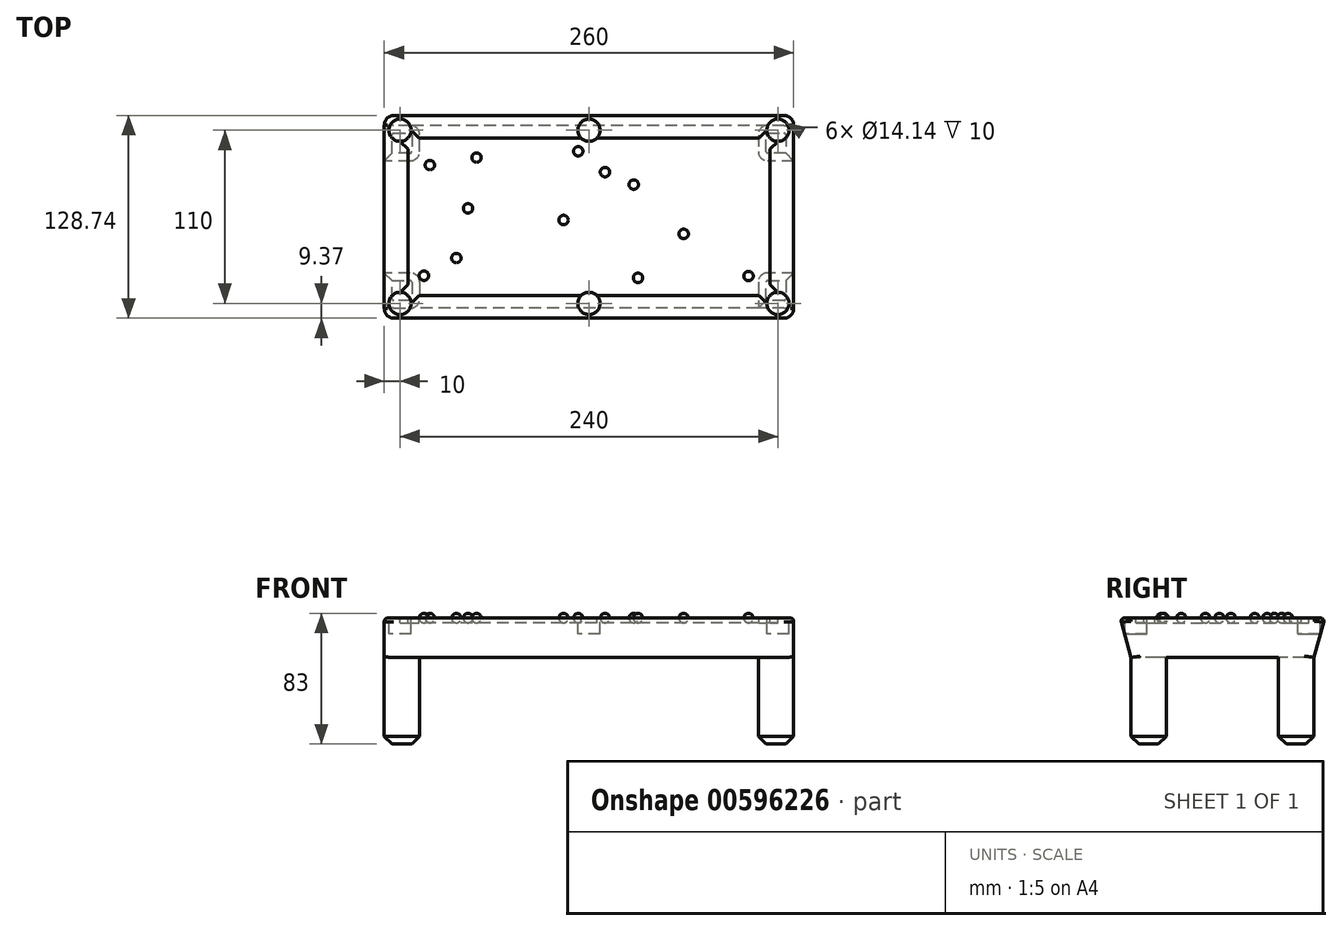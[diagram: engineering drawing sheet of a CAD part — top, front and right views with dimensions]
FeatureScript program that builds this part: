
annotation { "Feature Type Name" : "Feature", "Feature Type Description" : "" }
export const myFeature = defineFeature(function(context is Context, id is Id, definition is map)
    precondition{}
    {
        {
            var Q0;
            Q0=qCreatedBy(makeId("Top.planeOp"),FACE);
            var sketch = newSketch(context, id + "F0", { "sketchPlane" : qUnion([Q0])});
            skLineSegment(sketch, "E0.bottom", {"start": v(130, -65) * mm, "end": v(-130, -65) * mm});
            skLineSegment(sketch, "E0.top", {"start": v(130, 65) * mm, "end": v(-130, 65) * mm});
            skLineSegment(sketch, "E0.left", {"start": v(130, -65) * mm, "end": v(130, 65) * mm});
            skLineSegment(sketch, "E0.right", {"start": v(-130, -65) * mm, "end": v(-130, 65) * mm});
            skPoint(sketch, "E0.middle", {"position": v(0, 0) * mm});
            skLineSegment(sketch, "E1.bottom", {"start": v(112.93, -55) * mm, "end": v(7.07, -55) * mm});
            skLineSegment(sketch, "E1.top", {"start": v(112.93, 55) * mm, "end": v(7.07, 55) * mm});
            skLineSegment(sketch, "E1.left", {"start": v(120, -47.93) * mm, "end": v(120, 47.93) * mm});
            skLineSegment(sketch, "E1.right", {"start": v(-120, -47.93) * mm, "end": v(-120, 47.93) * mm});
            skLineSegment(sketch, "E2.bottom", {"start": v(107.93, -50) * mm, "end": v(5, -50) * mm});
            skLineSegment(sketch, "E2.top", {"start": v(107.93, 50) * mm, "end": v(5, 50) * mm});
            skLineSegment(sketch, "E2.left", {"start": v(115, -42.93) * mm, "end": v(115, 42.93) * mm});
            skLineSegment(sketch, "E2.right", {"start": v(-115, -42.93) * mm, "end": v(-115, 42.93) * mm});
            skCircle(sketch, "E3", {"center": v(120, 55) * mm, "radius": 7.07 * mm});
            skLineSegment(sketch, "E4", {"start": v(115, 42.93) * mm, "end": v(120, 47.93) * mm});
            skLineSegment(sketch, "E5", {"start": v(120, 47.93) * mm, "end": v(115, 42.93) * mm, "construction": true});
            skLineSegment(sketch, "E6", {"start": v(115, 42.93) * mm, "end": v(120, 42.93) * mm, "construction": true});
            skLineSegment(sketch, "E7", {"start": v(107.93, 50) * mm, "end": v(112.93, 55) * mm});
            skPoint(sketch, "E8.center.orphan", {"position": v(115, 50) * mm});
            skCircle(sketch, "E9", {"center": v(120, -55) * mm, "radius": 7.07 * mm});
            skCircle(sketch, "E10", {"center": v(-120, -55) * mm, "radius": 7.07 * mm});
            skCircle(sketch, "E11", {"center": v(-120, 55) * mm, "radius": 7.07 * mm});
            skCircle(sketch, "E12", {"center": v(0, -55) * mm, "radius": 7.07 * mm});
            skLineSegment(sketch, "E13", {"start": v(0, -47.93) * mm, "end": v(0, 47.93) * mm, "construction": true});
            skCircle(sketch, "E14", {"center": v(0, 55) * mm, "radius": 7.07 * mm});
            skLineSegment(sketch, "E15.trimOffspring", {"start": v(-7.07, 55) * mm, "end": v(-112.93, 55) * mm});
            skLineSegment(sketch, "E16.trimOffspring", {"start": v(-5, 50) * mm, "end": v(-107.93, 50) * mm});
            skLineSegment(sketch, "E17.trimOffspring", {"start": v(-7.07, -55) * mm, "end": v(-112.93, -55) * mm});
            skLineSegment(sketch, "E18.trimOffspring", {"start": v(-5, -50) * mm, "end": v(-107.93, -50) * mm});
            skLineSegment(sketch, "E19", {"start": v(107.93, -50) * mm, "end": v(112.93, -55) * mm});
            skLineSegment(sketch, "E20", {"start": v(115, -42.93) * mm, "end": v(120, -47.93) * mm});
            skLineSegment(sketch, "E21", {"start": v(-120, -47.93) * mm, "end": v(-115, -42.93) * mm});
            skLineSegment(sketch, "E22", {"start": v(-112.93, -55) * mm, "end": v(-107.93, -50) * mm});
            skPoint(sketch, "E23.orphan", {"position": v(-115, -50) * mm});
            skLineSegment(sketch, "E24", {"start": v(-120, 47.93) * mm, "end": v(-115, 42.93) * mm});
            skLineSegment(sketch, "E25", {"start": v(-112.93, 55) * mm, "end": v(-107.93, 50) * mm});
            skSolve(sketch);
        }
        {
            var Q0;
            Q0=qCreatedBy(makeId("Right.planeOp"),FACE);
            var sketch = newSketch(context, id + "F1", { "sketchPlane" : qUnion([Q0])});
            skLineSegment(sketch, "E26", {"start": v(58.07, -25) * mm, "end": v(-58.07, -25) * mm});
            skLineSegment(sketch, "E27.0", {"start": v(-65, 0) * mm, "end": v(65, 0) * mm});
            skLineSegment(sketch, "E28", {"start": v(58.07, -25) * mm, "end": v(65, 0) * mm});
            skLineSegment(sketch, "E29", {"start": v(-58.07, -25) * mm, "end": v(-65, 0) * mm});
            skLineSegment(sketch, "E30", {"start": v(58.07, -25) * mm, "end": v(58.07, -80) * mm});
            skLineSegment(sketch, "E31", {"start": v(58.07, -80) * mm, "end": v(-58.07, -80) * mm});
            skLineSegment(sketch, "E32", {"start": v(-58.07, -80) * mm, "end": v(-58.07, -25) * mm});
            skSolve(sketch);
        }
        {
            var Q0;
            Q0=makeQuery(id+"F1.imprint","IMPRINT",FACE,{"disambiguationData":[TD([[makeQuery(id+"F1.imprint","IMPRINT",EDGE,{"derivedFrom":sQuery(id+"F1.wireOp",EDGE,"E26")}),1.0]])]});
            var Q1;
            Q1=makeQuery(id+"F1.imprint","IMPRINT",FACE,{"disambiguationData":[TD([[makeQuery(id+"F1.imprint","IMPRINT",EDGE,{"derivedFrom":sQuery(id+"F1.wireOp",EDGE,"E26")}),-1.0]])]});
            extrude(context, id + "F2", {"entities" : qUnion([Q0, Q1]), "endBound" : BoundingType.SYMMETRIC, "depth" : 260 * mm, "offsetDistance" : 25 * mm});
        }
        {
            var Q0;
            Q0=makeQuery(id+"F2.opExtrude","SWEPT_FACE",FACE,{"disambiguationData":[OSD([sQuery(id+"F1.wireOp",EDGE,"E32")])]});
            var sketch = newSketch(context, id + "F3", { "sketchPlane" : qUnion([Q0])});
            skLineSegment(sketch, "E33.0", {"start": v(130, -80) * mm, "end": v(-130, -80) * mm});
            skLineSegment(sketch, "E34.0", {"start": v(130, -25) * mm, "end": v(-130, -25) * mm});
            skLineSegment(sketch, "E35", {"start": v(-107.5, -80) * mm, "end": v(-107.5, -25) * mm});
            skLineSegment(sketch, "E36", {"start": v(107.5, -80) * mm, "end": v(107.5, -25) * mm});
            skSolve(sketch);
        }
        {
            var Q0;
            {var subQ0=sQuery(id+"F3.wireOp",EDGE,"E35");Q0=makeQuery(id+"F3.imprint","IMPRINT",FACE,{"disambiguationData":[TD([[makeQuery(id+"F3.imprint","IMPRINT",EDGE,{"derivedFrom":subQ0}),-1.0]])]});}
            extrude(context, id + "F4", {"entities" : qUnion([Q0]), "operationType" : NewBodyOperationType.REMOVE, "oppositeDirection" : true, "depth" : 130 * mm, "offsetDistance" : 25 * mm});
        }
        {
            var Q0;
            Q0=makeQuery(id+"F2.opExtrude","CAP_FACE",FACE,{"disambiguationData":[OSD([sQuery(id+"F1.wireOp",EDGE,"E27.0"),sQuery(id+"F1.wireOp",EDGE,"E28"),sQuery(id+"F1.wireOp",EDGE,"E29"),sQuery(id+"F1.wireOp",EDGE,"E30"),sQuery(id+"F1.wireOp",EDGE,"E31"),sQuery(id+"F1.wireOp",EDGE,"E32")])],"isStart":true});
            var sketch = newSketch(context, id + "F5", { "sketchPlane" : qUnion([Q0])});
            skLineSegment(sketch, "E37.0", {"start": v(-58.07, -80) * mm, "end": v(58.07, -80) * mm});
            skLineSegment(sketch, "E38.0.0", {"start": v(58.07, -80) * mm, "end": v(58.07, -25) * mm});
            skLineSegment(sketch, "E38.0.1", {"start": v(58.07, -25) * mm, "end": v(65, 0) * mm});
            skLineSegment(sketch, "E38.0.2", {"start": v(65, 0) * mm, "end": v(-65, 0) * mm});
            skLineSegment(sketch, "E38.0.3", {"start": v(-65, 0) * mm, "end": v(-58.07, -25) * mm});
            skLineSegment(sketch, "E38.0.4", {"start": v(-58.07, -25) * mm, "end": v(-58.07, -80) * mm});
            skLineSegment(sketch, "E39", {"start": v(-58.07, -25) * mm, "end": v(58.07, -25) * mm});
            skLineSegment(sketch, "E40", {"start": v(-35.57, -80) * mm, "end": v(-35.57, -25) * mm});
            skLineSegment(sketch, "E41", {"start": v(35.57, -80) * mm, "end": v(35.57, -25) * mm});
            skSolve(sketch);
        }
        {
            var Q0;
            {var subQ0=sQuery(id+"F5.wireOp",EDGE,"E40");Q0=makeQuery(id+"F5.imprint","IMPRINT",FACE,{"disambiguationData":[TD([[makeQuery(id+"F5.imprint","IMPRINT",EDGE,{"derivedFrom":subQ0}),-1.0]])]});}
            extrude(context, id + "F6", {"entities" : qUnion([Q0]), "operationType" : NewBodyOperationType.REMOVE, "oppositeDirection" : true, "depth" : 260 * mm, "offsetDistance" : 25 * mm});
        }
        {
            var Q0;
            {var subQ0=sQuery(id+"F0.wireOp",EDGE,"E9");var subQ1=makeQuery(id+"F0.imprint","INTERSECT",VERTEX,{"derivedFrom":[sQuery(id+"F0.wireOp",EDGE,"E1.bottom"),subQ0,sQuery(id+"F0.wireOp",EDGE,"E19")]});Q0=makeQuery(id+"F0.imprint","IMPRINT",FACE,{"disambiguationData":[TD([[makeQuery(id+"F0.imprint","IMPRINT",EDGE,{"disambiguationData":[TD([[subQ1,1.0]])],"derivedFrom":subQ0}),1.0]])]});}
            var Q1;
            {var subQ0=sQuery(id+"F0.wireOp",EDGE,"E3");var subQ1=makeQuery(id+"F0.imprint","INTERSECT",VERTEX,{"derivedFrom":[sQuery(id+"F0.wireOp",EDGE,"E1.top"),subQ0,sQuery(id+"F0.wireOp",EDGE,"E7")]});Q1=makeQuery(id+"F0.imprint","IMPRINT",FACE,{"disambiguationData":[TD([[makeQuery(id+"F0.imprint","IMPRINT",EDGE,{"disambiguationData":[TD([[subQ1,-1.0]])],"derivedFrom":subQ0}),1.0]])]});}
            var Q2;
            {var subQ0=sQuery(id+"F0.wireOp",EDGE,"E14");var subQ1=makeQuery(id+"F0.imprint","INTERSECT",VERTEX,{"derivedFrom":[sQuery(id+"F0.wireOp",EDGE,"E1.top"),subQ0]});Q2=makeQuery(id+"F0.imprint","IMPRINT",FACE,{"disambiguationData":[TD([[makeQuery(id+"F0.imprint","IMPRINT",EDGE,{"disambiguationData":[TD([[subQ1,-1.0]])],"derivedFrom":subQ0}),1.0]])]});}
            var Q3;
            {var subQ0=sQuery(id+"F0.wireOp",EDGE,"E12");var subQ1=makeQuery(id+"F0.imprint","INTERSECT",VERTEX,{"derivedFrom":[sQuery(id+"F0.wireOp",EDGE,"E1.bottom"),subQ0]});Q3=makeQuery(id+"F0.imprint","IMPRINT",FACE,{"disambiguationData":[TD([[makeQuery(id+"F0.imprint","IMPRINT",EDGE,{"disambiguationData":[TD([[subQ1,-1.0]])],"derivedFrom":subQ0}),1.0]])]});}
            var Q4;
            {var subQ0=sQuery(id+"F0.wireOp",EDGE,"E10");var subQ1=makeQuery(id+"F0.imprint","INTERSECT",VERTEX,{"derivedFrom":[sQuery(id+"F0.wireOp",EDGE,"E1.right"),subQ0,sQuery(id+"F0.wireOp",EDGE,"E21")]});Q4=makeQuery(id+"F0.imprint","IMPRINT",FACE,{"disambiguationData":[TD([[makeQuery(id+"F0.imprint","IMPRINT",EDGE,{"disambiguationData":[TD([[subQ1,1.0]])],"derivedFrom":subQ0}),1.0]])]});}
            var Q5;
            {var subQ0=sQuery(id+"F0.wireOp",EDGE,"E11");var subQ1=makeQuery(id+"F0.imprint","INTERSECT",VERTEX,{"derivedFrom":[sQuery(id+"F0.wireOp",EDGE,"E1.right"),subQ0,sQuery(id+"F0.wireOp",EDGE,"E24")]});Q5=makeQuery(id+"F0.imprint","IMPRINT",FACE,{"disambiguationData":[TD([[makeQuery(id+"F0.imprint","IMPRINT",EDGE,{"disambiguationData":[TD([[subQ1,1.0]])],"derivedFrom":subQ0}),1.0]])]});}
            extrude(context, id + "F7", {"entities" : qUnion([Q0, Q1, Q2, Q3, Q4, Q5]), "operationType" : NewBodyOperationType.REMOVE, "oppositeDirection" : true, "depth" : 10 * mm, "offsetDistance" : 25 * mm});
        }
        {
            var Q0;
            {var subQ13=sQuery(id+"F0.wireOp",EDGE,"E2.bottom");Q0=makeQuery(id+"F0.imprint","IMPRINT",FACE,{"disambiguationData":[TD([[makeQuery(id+"F0.imprint","IMPRINT",EDGE,{"derivedFrom":subQ13}),-1.0]])]});}
            extrude(context, id + "F8", {"entities" : qUnion([Q0]), "operationType" : NewBodyOperationType.REMOVE, "oppositeDirection" : true, "depth" : 3 * mm, "offsetDistance" : 25 * mm});
        }
        {
            var Q0;
            Q0=makeQuery(id+"F2.opExtrude","CAP_EDGE",EDGE,{"disambiguationData":[OSD([sQuery(id+"F1.wireOp",EDGE,"E28")])],"isStart":false});
            fillet(context, id + "F9", {"entities" : qUnion([Q0]), "radius" : 6 * mm, "tangentPropagation" : true, "allowEdgeOverflow" : false});
        }
        {
            var Q0;
            Q0=makeQuery(id+"F2.opExtrude","CAP_EDGE",EDGE,{"disambiguationData":[OSD([sQuery(id+"F1.wireOp",EDGE,"E29")])],"isStart":false});
            var Q1;
            Q1=makeQuery(id+"F2.opExtrude","CAP_EDGE",EDGE,{"disambiguationData":[OSD([sQuery(id+"F1.wireOp",EDGE,"E29")])],"isStart":true});
            var Q2;
            Q2=makeQuery(id+"F2.opExtrude","CAP_EDGE",EDGE,{"disambiguationData":[OSD([sQuery(id+"F1.wireOp",EDGE,"E28")])],"isStart":true});
            fillet(context, id + "F10", {"entities" : qUnion([Q0, Q1, Q2]), "radius" : 6 * mm, "tangentPropagation" : true, "allowEdgeOverflow" : false});
        }
        {
            var Q0;
            Q0=makeQuery(id+"F2.opExtrude","CAP_EDGE",EDGE,{"disambiguationData":[OSD([sQuery(id+"F1.wireOp",EDGE,"E32")])],"isStart":false});
            var Q1;
            Q1=makeQuery(id+"F2.opExtrude","CAP_EDGE",EDGE,{"disambiguationData":[OSD([sQuery(id+"F1.wireOp",EDGE,"E30")])],"isStart":false});
            var Q2;
            Q2=makeQuery(id+"F2.opExtrude","CAP_EDGE",EDGE,{"disambiguationData":[OSD([sQuery(id+"F1.wireOp",EDGE,"E32")])],"isStart":true});
            var Q3;
            Q3=makeQuery(id+"F2.opExtrude","CAP_EDGE",EDGE,{"disambiguationData":[OSD([sQuery(id+"F1.wireOp",EDGE,"E30")])],"isStart":true});
            fillet(context, id + "F11", {"entities" : qUnion([Q0, Q1, Q2, Q3]), "radius" : 6 * mm, "tangentPropagation" : true, "allowEdgeOverflow" : false});
        }
        {
            var Q0;
            Q0=makeQuery(id+"F2.opExtrude","SWEPT_EDGE",EDGE,{"disambiguationData":[OSD([sQuery(id+"F1.wireOp",EDGE,"E27.0"),sQuery(id+"F1.wireOp",EDGE,"E29")])]});
            var Q1;
            Q1=makeQuery(id+"F2.opExtrude","CAP_EDGE",EDGE,{"disambiguationData":[OSD([sQuery(id+"F1.wireOp",EDGE,"E27.0")])],"isStart":true});
            fillet(context, id + "F12", {"entities" : qUnion([Q0, Q1]), "radius" : 2 * mm, "tangentPropagation" : true, "allowEdgeOverflow" : false});
        }
        {
            var Q0;
            Q0=qCreatedBy(makeId("Top.planeOp"),FACE);
            var sketch = newSketch(context, id + "F13", { "sketchPlane" : qUnion([Q0])});
            skCircle(sketch, "E42", {"center": v(-71.42, 37.6) * mm, "radius": 3 * mm});
            skLineSegment(sketch, "E43", {"start": v(-71.42, 34.6) * mm, "end": v(-71.42, 40.6) * mm});
            skCircle(sketch, "E44", {"center": v(-84.23, -26.2) * mm, "radius": 3 * mm});
            skLineSegment(sketch, "E45", {"start": v(-84.23, -29.2) * mm, "end": v(-84.23, -23.2) * mm});
            skCircle(sketch, "E46", {"center": v(31.13, -38.8) * mm, "radius": 3 * mm});
            skLineSegment(sketch, "E47", {"start": v(31.13, -41.8) * mm, "end": v(31.13, -35.8) * mm});
            skCircle(sketch, "E48", {"center": v(-16.15, -2.03) * mm, "radius": 3 * mm});
            skLineSegment(sketch, "E49", {"start": v(-16.15, -5.03) * mm, "end": v(-16.15, 0.97) * mm});
            skCircle(sketch, "E50", {"center": v(28.4, 20.46) * mm, "radius": 3 * mm});
            skLineSegment(sketch, "E51", {"start": v(28.4, 17.46) * mm, "end": v(28.4, 23.46) * mm});
            skCircle(sketch, "E52", {"center": v(-6.85, 41.64) * mm, "radius": 3 * mm});
            skLineSegment(sketch, "E53", {"start": v(-6.85, 38.64) * mm, "end": v(-6.85, 44.64) * mm});
            skCircle(sketch, "E54", {"center": v(101.35, -37.6) * mm, "radius": 3 * mm});
            skLineSegment(sketch, "E55", {"start": v(101.35, -40.6) * mm, "end": v(101.35, -34.6) * mm});
            skCircle(sketch, "E56", {"center": v(-101.07, 32.85) * mm, "radius": 3 * mm});
            skLineSegment(sketch, "E57", {"start": v(-101.07, 29.85) * mm, "end": v(-101.07, 35.85) * mm});
            skCircle(sketch, "E58", {"center": v(-104.83, -37.39) * mm, "radius": 3 * mm});
            skLineSegment(sketch, "E59", {"start": v(-104.83, -40.39) * mm, "end": v(-104.83, -34.39) * mm});
            skCircle(sketch, "E60", {"center": v(10.14, 28.37) * mm, "radius": 3 * mm});
            skLineSegment(sketch, "E61", {"start": v(10.14, 25.37) * mm, "end": v(10.14, 31.37) * mm});
            skCircle(sketch, "E62", {"center": v(-76.83, 5.36) * mm, "radius": 3 * mm});
            skLineSegment(sketch, "E63", {"start": v(-76.83, 2.36) * mm, "end": v(-76.83, 8.36) * mm});
            skCircle(sketch, "E64", {"center": v(60.12, -10.86) * mm, "radius": 3 * mm});
            skLineSegment(sketch, "E65", {"start": v(60.12, -13.86) * mm, "end": v(60.12, -7.86) * mm});
            skSolve(sketch);
        }
        {
            var Q0;
            {var subQ0=sQuery(id+"F13.wireOp",EDGE,"E43");Q0=makeQuery(id+"F13.imprint","IMPRINT",FACE,{"disambiguationData":[TD([[makeQuery(id+"F13.imprint","IMPRINT",EDGE,{"derivedFrom":subQ0}),-1.0]])]});}
            var Q1;
            Q1=sQuery(id+"F13.wireOp",EDGE,"E43");
            revolve(context, id + "F14", {"entities" : qUnion([Q0]), "axis" : qUnion([Q1]), "revolveType" : RevolveType.FULL});
        }
        {
            var Q0;
            {var subQ0=sQuery(id+"F13.wireOp",EDGE,"E49");Q0=makeQuery(id+"F13.imprint","IMPRINT",FACE,{"disambiguationData":[TD([[makeQuery(id+"F13.imprint","IMPRINT",EDGE,{"derivedFrom":subQ0}),-1.0]])]});}
            var Q1;
            Q1=sQuery(id+"F13.wireOp",EDGE,"E49");
            revolve(context, id + "F15", {"entities" : qUnion([Q0]), "axis" : qUnion([Q1]), "revolveType" : RevolveType.FULL});
        }
        {
            var Q0;
            {var subQ0=sQuery(id+"F13.wireOp",EDGE,"E63");Q0=makeQuery(id+"F13.imprint","IMPRINT",FACE,{"disambiguationData":[TD([[makeQuery(id+"F13.imprint","IMPRINT",EDGE,{"derivedFrom":subQ0}),-1.0]])]});}
            var Q1;
            Q1=sQuery(id+"F13.wireOp",EDGE,"E56");
            var Q2;
            Q2=sQuery(id+"F13.wireOp",EDGE,"E63");
            revolve(context, id + "F16", {"entities" : qUnion([Q0]), "surfaceEntities" : qUnion([Q1]), "axis" : qUnion([Q2]), "revolveType" : RevolveType.FULL});
        }
        {
            var Q0;
            {var subQ0=sQuery(id+"F13.wireOp",EDGE,"E53");Q0=makeQuery(id+"F13.imprint","IMPRINT",FACE,{"disambiguationData":[TD([[makeQuery(id+"F13.imprint","IMPRINT",EDGE,{"derivedFrom":subQ0}),-1.0]])]});}
            var Q1;
            Q1=sQuery(id+"F13.wireOp",EDGE,"E53");
            revolve(context, id + "F17", {"entities" : qUnion([Q0]), "axis" : qUnion([Q1]), "revolveType" : RevolveType.FULL});
        }
        {
            var Q0;
            {var subQ0=sQuery(id+"F13.wireOp",EDGE,"E51");Q0=makeQuery(id+"F13.imprint","IMPRINT",FACE,{"disambiguationData":[TD([[makeQuery(id+"F13.imprint","IMPRINT",EDGE,{"derivedFrom":subQ0}),-1.0]])]});}
            var Q1;
            Q1=sQuery(id+"F13.wireOp",EDGE,"E51");
            revolve(context, id + "F18", {"entities" : qUnion([Q0]), "axis" : qUnion([Q1]), "revolveType" : RevolveType.FULL});
        }
        {
            var Q0;
            {var subQ0=sQuery(id+"F13.wireOp",EDGE,"E47");Q0=makeQuery(id+"F13.imprint","IMPRINT",FACE,{"disambiguationData":[TD([[makeQuery(id+"F13.imprint","IMPRINT",EDGE,{"derivedFrom":subQ0}),-1.0]])]});}
            var Q1;
            Q1=sQuery(id+"F13.wireOp",EDGE,"E47");
            revolve(context, id + "F19", {"entities" : qUnion([Q0]), "axis" : qUnion([Q1]), "revolveType" : RevolveType.FULL});
        }
        {
            var Q0;
            {var subQ0=sQuery(id+"F13.wireOp",EDGE,"E55");Q0=makeQuery(id+"F13.imprint","IMPRINT",FACE,{"disambiguationData":[TD([[makeQuery(id+"F13.imprint","IMPRINT",EDGE,{"derivedFrom":subQ0}),1.0]])]});}
            var Q1;
            Q1=sQuery(id+"F13.wireOp",EDGE,"E55");
            revolve(context, id + "F20", {"entities" : qUnion([Q0]), "axis" : qUnion([Q1]), "revolveType" : RevolveType.FULL});
        }
        {
            var Q0;
            {var subQ0=sQuery(id+"F13.wireOp",EDGE,"E45");Q0=makeQuery(id+"F13.imprint","IMPRINT",FACE,{"disambiguationData":[TD([[makeQuery(id+"F13.imprint","IMPRINT",EDGE,{"derivedFrom":subQ0}),1.0]])]});}
            var Q1;
            Q1=sQuery(id+"F13.wireOp",EDGE,"E45");
            revolve(context, id + "F21", {"entities" : qUnion([Q0]), "axis" : qUnion([Q1]), "revolveType" : RevolveType.FULL});
        }
        {
            var Q0;
            {var subQ0=sQuery(id+"F13.wireOp",EDGE,"E61");Q0=makeQuery(id+"F13.imprint","IMPRINT",FACE,{"disambiguationData":[TD([[makeQuery(id+"F13.imprint","IMPRINT",EDGE,{"derivedFrom":subQ0}),-1.0]])]});}
            var Q1;
            Q1=sQuery(id+"F13.wireOp",EDGE,"E61");
            revolve(context, id + "F22", {"entities" : qUnion([Q0]), "axis" : qUnion([Q1]), "revolveType" : RevolveType.FULL});
        }
        {
            var Q0;
            {var subQ0=sQuery(id+"F13.wireOp",EDGE,"E57");Q0=makeQuery(id+"F13.imprint","IMPRINT",FACE,{"disambiguationData":[TD([[makeQuery(id+"F13.imprint","IMPRINT",EDGE,{"derivedFrom":subQ0}),1.0]])]});}
            var Q1;
            Q1=sQuery(id+"F13.wireOp",EDGE,"E57");
            revolve(context, id + "F23", {"entities" : qUnion([Q0]), "axis" : qUnion([Q1]), "revolveType" : RevolveType.FULL});
        }
        {
            var Q0;
            {var subQ0=sQuery(id+"F13.wireOp",EDGE,"E65");Q0=makeQuery(id+"F13.imprint","IMPRINT",FACE,{"disambiguationData":[TD([[makeQuery(id+"F13.imprint","IMPRINT",EDGE,{"derivedFrom":subQ0}),1.0]])]});}
            var Q1;
            Q1=sQuery(id+"F13.wireOp",EDGE,"E65");
            revolve(context, id + "F24", {"entities" : qUnion([Q0]), "axis" : qUnion([Q1]), "revolveType" : RevolveType.FULL});
        }
        {
            var Q0;
            {var subQ0=sQuery(id+"F13.wireOp",EDGE,"E59");Q0=makeQuery(id+"F13.imprint","IMPRINT",FACE,{"disambiguationData":[TD([[makeQuery(id+"F13.imprint","IMPRINT",EDGE,{"derivedFrom":subQ0}),-1.0]])]});}
            var Q1;
            Q1=sQuery(id+"F13.wireOp",EDGE,"E59");
            revolve(context, id + "F25", {"entities" : qUnion([Q0]), "axis" : qUnion([Q1]), "revolveType" : RevolveType.FULL});
        }
        {
            var Q0;
            Q0=makeQuery(id+"F4.boolean.opBoolean","COPY",EDGE,{"derivedFrom":makeQuery(id+"F4.opExtrude","CAP_EDGE",EDGE,{"disambiguationData":[OSD([sQuery(id+"F3.wireOp",EDGE,"E35")])],"isStart":true})});
            var Q1;
            Q1=makeQuery(id+"F6.boolean.opBoolean","INTERSECT",EDGE,{"derivedFrom":[makeQuery(id+"F4.boolean.opBoolean","COPY",FACE,{"derivedFrom":makeQuery(id+"F4.opExtrude","SWEPT_FACE",FACE,{"disambiguationData":[OSD([sQuery(id+"F3.wireOp",EDGE,"E35")])]})}),makeQuery(id+"F6.opExtrude","SWEPT_FACE",FACE,{"disambiguationData":[OSD([sQuery(id+"F5.wireOp",EDGE,"E41")])]})]});
            var Q2;
            Q2=makeQuery(id+"F6.boolean.opBoolean","INTERSECT",EDGE,{"derivedFrom":[makeQuery(id+"F4.boolean.opBoolean","COPY",FACE,{"derivedFrom":makeQuery(id+"F4.opExtrude","SWEPT_FACE",FACE,{"disambiguationData":[OSD([sQuery(id+"F3.wireOp",EDGE,"E35")])]})}),makeQuery(id+"F6.opExtrude","SWEPT_FACE",FACE,{"disambiguationData":[OSD([sQuery(id+"F5.wireOp",EDGE,"E40")])]})]});
            var Q3;
            Q3=makeQuery(id+"F6.boolean.opBoolean","COPY",EDGE,{"derivedFrom":makeQuery(id+"F6.opExtrude","CAP_EDGE",EDGE,{"disambiguationData":[OSD([sQuery(id+"F5.wireOp",EDGE,"E40")])],"isStart":true})});
            var Q4;
            Q4=makeQuery(id+"F4.boolean.opBoolean","INTERSECT",EDGE,{"derivedFrom":[makeQuery(id+"F2.opExtrude","SWEPT_FACE",FACE,{"disambiguationData":[OSD([sQuery(id+"F1.wireOp",EDGE,"E30")])]}),makeQuery(id+"F4.opExtrude","SWEPT_FACE",FACE,{"disambiguationData":[OSD([sQuery(id+"F3.wireOp",EDGE,"E35")])]})]});
            var Q5;
            Q5=makeQuery(id+"F4.boolean.opBoolean","COPY",EDGE,{"derivedFrom":makeQuery(id+"F4.opExtrude","CAP_EDGE",EDGE,{"disambiguationData":[OSD([sQuery(id+"F3.wireOp",EDGE,"E36")])],"isStart":true})});
            var Q6;
            Q6=makeQuery(id+"F6.boolean.opBoolean","COPY",EDGE,{"derivedFrom":makeQuery(id+"F6.opExtrude","CAP_EDGE",EDGE,{"disambiguationData":[OSD([sQuery(id+"F5.wireOp",EDGE,"E41")])],"isStart":false})});
            var Q7;
            Q7=makeQuery(id+"F6.boolean.opBoolean","INTERSECT",EDGE,{"derivedFrom":[makeQuery(id+"F4.boolean.opBoolean","COPY",FACE,{"derivedFrom":makeQuery(id+"F4.opExtrude","SWEPT_FACE",FACE,{"disambiguationData":[OSD([sQuery(id+"F3.wireOp",EDGE,"E36")])]})}),makeQuery(id+"F6.opExtrude","SWEPT_FACE",FACE,{"disambiguationData":[OSD([sQuery(id+"F5.wireOp",EDGE,"E40")])]})]});
            var Q8;
            Q8=makeQuery(id+"F6.boolean.opBoolean","COPY",EDGE,{"derivedFrom":makeQuery(id+"F6.opExtrude","CAP_EDGE",EDGE,{"disambiguationData":[OSD([sQuery(id+"F5.wireOp",EDGE,"E40")])],"isStart":false})});
            var Q9;
            Q9=makeQuery(id+"F6.boolean.opBoolean","INTERSECT",EDGE,{"derivedFrom":[makeQuery(id+"F4.boolean.opBoolean","COPY",FACE,{"derivedFrom":makeQuery(id+"F4.opExtrude","SWEPT_FACE",FACE,{"disambiguationData":[OSD([sQuery(id+"F3.wireOp",EDGE,"E36")])]})}),makeQuery(id+"F6.opExtrude","SWEPT_FACE",FACE,{"disambiguationData":[OSD([sQuery(id+"F5.wireOp",EDGE,"E41")])]})]});
            var Q10;
            Q10=makeQuery(id+"F4.boolean.opBoolean","INTERSECT",EDGE,{"derivedFrom":[makeQuery(id+"F2.opExtrude","SWEPT_FACE",FACE,{"disambiguationData":[OSD([sQuery(id+"F1.wireOp",EDGE,"E30")])]}),makeQuery(id+"F4.opExtrude","SWEPT_FACE",FACE,{"disambiguationData":[OSD([sQuery(id+"F3.wireOp",EDGE,"E36")])]})]});
            var Q11;
            Q11=makeQuery(id+"F6.boolean.opBoolean","COPY",EDGE,{"derivedFrom":makeQuery(id+"F6.opExtrude","CAP_EDGE",EDGE,{"disambiguationData":[OSD([sQuery(id+"F5.wireOp",EDGE,"E41")])],"isStart":true})});
            fillet(context, id + "F26", {"entities" : qUnion([Q0, Q1, Q2, Q3, Q4, Q5, Q6, Q7, Q8, Q9, Q10, Q11]), "radius" : 6 * mm, "tangentPropagation" : true, "allowEdgeOverflow" : false});
        }
        {
            var Q0;
            {var subQ0=sQuery(id+"F1.wireOp",EDGE,"E32");var subQ1=sQuery(id+"F1.wireOp",EDGE,"E31");var subQ4=makeQuery(id+"F2.opExtrude","SWEPT_FACE",FACE,{"disambiguationData":[OSD([subQ0])]});var subQ5=makeQuery(id+"F4.opExtrude","SWEPT_FACE",FACE,{"disambiguationData":[OSD([sQuery(id+"F3.wireOp",EDGE,"E36")])]});Q0=makeQuery(id+"F6.boolean.opBoolean","SPLIT",FACE,{"disambiguationData":[TD([subQ4])],"derivedFrom":makeQuery(id+"F4.boolean.opBoolean","SPLIT",FACE,{"disambiguationData":[TD([subQ5])],"derivedFrom":makeQuery(id+"F2.opExtrude","SWEPT_FACE",FACE,{"disambiguationData":[OSD([subQ1])]})})});}
            var Q1;
            {var subQ0=sQuery(id+"F1.wireOp",EDGE,"E32");var subQ1=sQuery(id+"F1.wireOp",EDGE,"E31");var subQ4=makeQuery(id+"F2.opExtrude","SWEPT_FACE",FACE,{"disambiguationData":[OSD([subQ0])]});var subQ5=makeQuery(id+"F4.opExtrude","SWEPT_FACE",FACE,{"disambiguationData":[OSD([sQuery(id+"F3.wireOp",EDGE,"E35")])]});Q1=makeQuery(id+"F6.boolean.opBoolean","SPLIT",FACE,{"disambiguationData":[TD([subQ4])],"derivedFrom":makeQuery(id+"F4.boolean.opBoolean","SPLIT",FACE,{"disambiguationData":[TD([subQ5])],"derivedFrom":makeQuery(id+"F2.opExtrude","SWEPT_FACE",FACE,{"disambiguationData":[OSD([subQ1])]})})});}
            var Q2;
            {var subQ1=sQuery(id+"F5.wireOp",EDGE,"E40");Q2=makeQuery(id+"F6.boolean.opBoolean","COPY",EDGE,{"disambiguationData":[TD([makeQuery(id+"F4.boolean.opBoolean","COPY",FACE,{"derivedFrom":makeQuery(id+"F4.opExtrude","SWEPT_FACE",FACE,{"disambiguationData":[OSD([sQuery(id+"F3.wireOp",EDGE,"E35")])]})})])],"derivedFrom":makeQuery(id+"F6.opExtrude","SWEPT_EDGE",EDGE,{"disambiguationData":[OSD([sQuery(id+"F5.wireOp",EDGE,"E37.0"),subQ1])]})});}
            var Q3;
            {var subQ1=sQuery(id+"F1.wireOp",EDGE,"E31");var subQ2=sQuery(id+"F1.wireOp",EDGE,"E30");var subQ4=makeQuery(id+"F2.opExtrude","SWEPT_FACE",FACE,{"disambiguationData":[OSD([subQ2])]});var subQ5=makeQuery(id+"F4.opExtrude","SWEPT_FACE",FACE,{"disambiguationData":[OSD([sQuery(id+"F3.wireOp",EDGE,"E36")])]});Q3=makeQuery(id+"F6.boolean.opBoolean","SPLIT",FACE,{"disambiguationData":[TD([subQ4])],"derivedFrom":makeQuery(id+"F4.boolean.opBoolean","SPLIT",FACE,{"disambiguationData":[TD([subQ5])],"derivedFrom":makeQuery(id+"F2.opExtrude","SWEPT_FACE",FACE,{"disambiguationData":[OSD([subQ1])]})})});}
            chamfer(context, id + "F27", {"entities" : qUnion([Q0, Q1, Q2, Q3]), "width" : 5 * mm, "tangentPropagation" : true});
        }
    });
